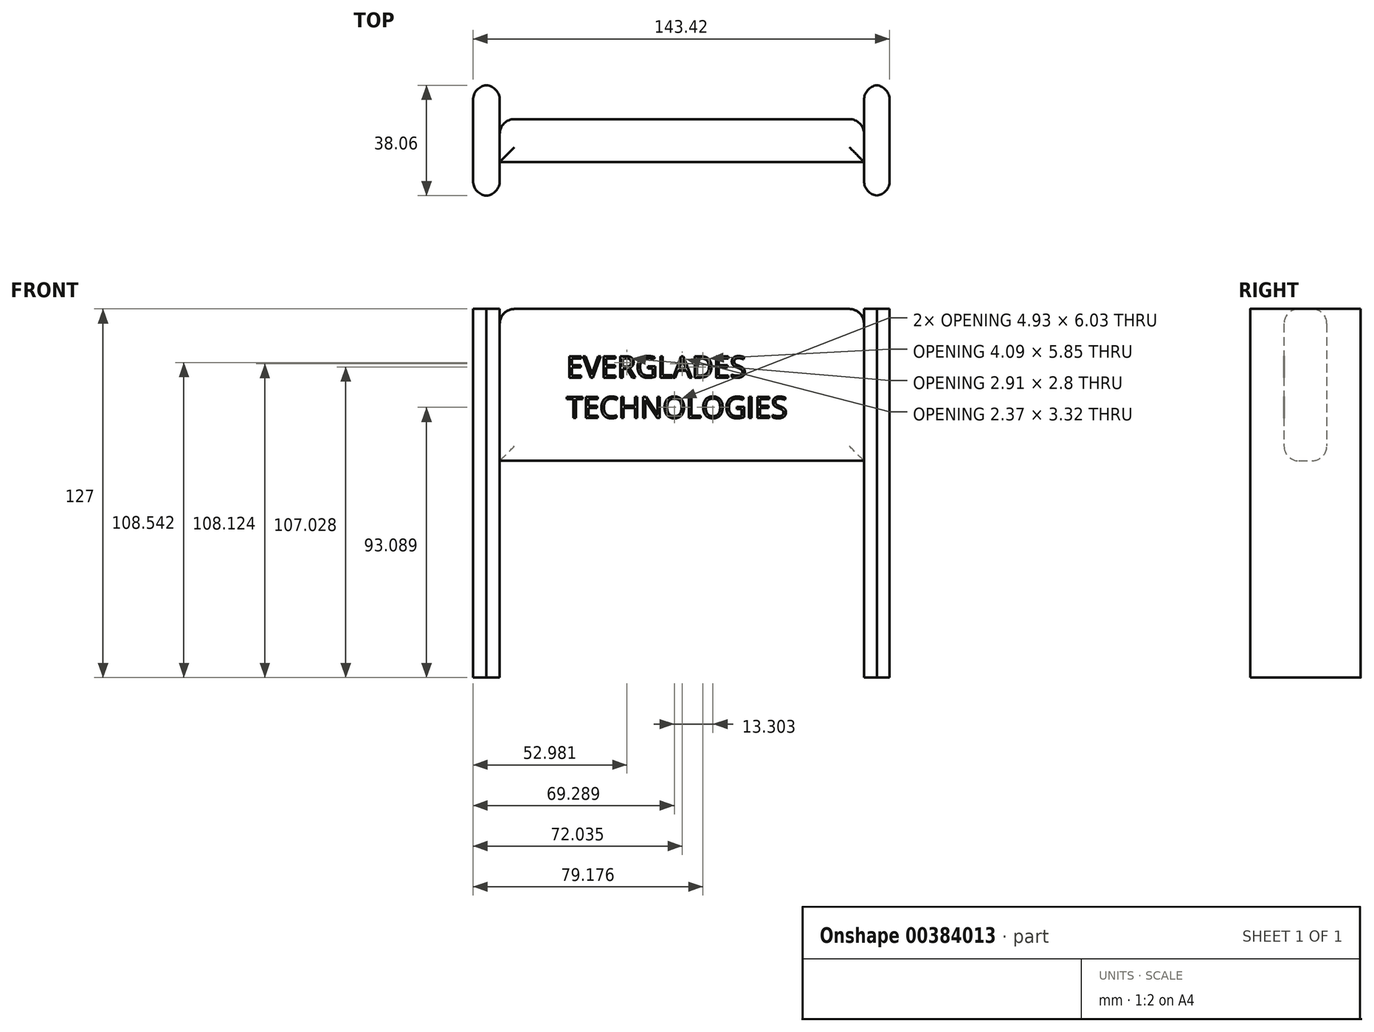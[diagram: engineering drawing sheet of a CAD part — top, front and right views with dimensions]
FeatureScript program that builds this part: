
annotation { "Feature Type Name" : "Feature", "Feature Type Description" : "" }
export const myFeature = defineFeature(function(context is Context, id is Id, definition is map)
    precondition{}
    {
        {
            var Q0;
            Q0=qCreatedBy(makeId("Front.planeOp"),FACE);
            var sketch = newSketch(context, id + "F0", { "sketchPlane" : qUnion([Q0])});
            skLineSegment(sketch, "E0.bottom", {"start": v(-58.02, 63.98) * mm, "end": v(67.38, 63.98) * mm});
            skLineSegment(sketch, "E0.top", {"start": v(-58.02, 11.67) * mm, "end": v(67.38, 11.67) * mm});
            skLineSegment(sketch, "E0.left", {"start": v(-58.02, 63.98) * mm, "end": v(-58.02, 11.67) * mm});
            skLineSegment(sketch, "E0.right", {"start": v(67.38, 63.98) * mm, "end": v(67.38, 11.67) * mm});
            skLineSegment(sketch, "E1", {"start": v(-58.02, 11.67) * mm, "end": v(-58.02, -63.02) * mm});
            skLineSegment(sketch, "E2", {"start": v(-67.23, 63.98) * mm, "end": v(-67.23, -63.02) * mm});
            skLineSegment(sketch, "E3", {"start": v(67.38, 11.67) * mm, "end": v(67.38, -63.02) * mm});
            skLineSegment(sketch, "E4", {"start": v(76.2, 63.98) * mm, "end": v(76.2, -63.02) * mm});
            skLineSegment(sketch, "E5", {"start": v(-67.23, 63.98) * mm, "end": v(-58.02, 63.98) * mm});
            skLineSegment(sketch, "E6", {"start": v(67.38, 63.98) * mm, "end": v(76.2, 63.98) * mm});
            skLineSegment(sketch, "E7", {"start": v(67.38, -63.02) * mm, "end": v(76.2, -63.02) * mm});
            skLineSegment(sketch, "E8", {"start": v(-67.23, -63.02) * mm, "end": v(-58.02, -63.02) * mm});
            skSolve(sketch);
        }
        {
            var Q0;
            Q0=makeQuery(id+"F0.imprint","IMPRINT",FACE,{"disambiguationData":[TD([[makeQuery(id+"F0.imprint","IMPRINT",EDGE,{"derivedFrom":sQuery(id+"F0.wireOp",EDGE,"E0.left")}),-1.0]])]});
            var Q1;
            Q1=makeQuery(id+"F0.imprint","IMPRINT",FACE,{"disambiguationData":[TD([[makeQuery(id+"F0.imprint","IMPRINT",EDGE,{"derivedFrom":sQuery(id+"F0.wireOp",EDGE,"E0.right")}),1.0]])]});
            extrude(context, id + "F1", {"entities" : qUnion([Q0, Q1]), "endBound" : BoundingType.SYMMETRIC, "depth" : 38.1 * mm});
        }
        {
            var Q0;
            Q0=makeQuery(id+"F0.imprint","IMPRINT",FACE,{"disambiguationData":[TD([[makeQuery(id+"F0.imprint","IMPRINT",EDGE,{"derivedFrom":sQuery(id+"F0.wireOp",EDGE,"E0.bottom")}),-1.0]])]});
            extrude(context, id + "F2", {"entities" : qUnion([Q0]), "endBound" : BoundingType.SYMMETRIC, "depth" : 14.73 * mm});
        }
        {
            var Q0;
            Q0=makeQuery(id+"F1.opExtrude","CAP_EDGE",EDGE,{"disambiguationData":[OSD([sQuery(id+"F0.wireOp",EDGE,"E2")])],"isStart":false});
            var Q1;
            Q1=makeQuery(id+"F1.opExtrude","CAP_EDGE",EDGE,{"disambiguationData":[OSD([sQuery(id+"F0.wireOp",EDGE,"E0.left"),sQuery(id+"F0.wireOp",EDGE,"E1")])],"isStart":false});
            var Q2;
            Q2=makeQuery(id+"F2.opExtrude","SWEPT_EDGE",EDGE,{"disambiguationData":[OSD([sQuery(id+"F0.wireOp",EDGE,"E0.bottom"),sQuery(id+"F0.wireOp",EDGE,"E0.left"),sQuery(id+"F0.wireOp",EDGE,"E5")])]});
            var Q3;
            Q3=makeQuery(id+"F2.opExtrude","CAP_EDGE",EDGE,{"disambiguationData":[OSD([sQuery(id+"F0.wireOp",EDGE,"E0.bottom")])],"isStart":false});
            var Q4;
            Q4=makeQuery(id+"F2.opExtrude","CAP_EDGE",EDGE,{"disambiguationData":[OSD([sQuery(id+"F0.wireOp",EDGE,"E0.top")])],"isStart":false});
            var Q5;
            Q5=makeQuery(id+"F1.opExtrude","CAP_EDGE",EDGE,{"disambiguationData":[OSD([sQuery(id+"F0.wireOp",EDGE,"E2")])],"isStart":true});
            var Q6;
            Q6=makeQuery(id+"F1.opExtrude","CAP_EDGE",EDGE,{"disambiguationData":[OSD([sQuery(id+"F0.wireOp",EDGE,"E0.left"),sQuery(id+"F0.wireOp",EDGE,"E1")])],"isStart":true});
            var Q7;
            Q7=makeQuery(id+"F1.opExtrude","CAP_EDGE",EDGE,{"disambiguationData":[OSD([sQuery(id+"F0.wireOp",EDGE,"E4")])],"isStart":false});
            var Q8;
            Q8=makeQuery(id+"F1.opExtrude","CAP_EDGE",EDGE,{"disambiguationData":[OSD([sQuery(id+"F0.wireOp",EDGE,"E0.right"),sQuery(id+"F0.wireOp",EDGE,"E3")])],"isStart":false});
            var Q9;
            Q9=makeQuery(id+"F1.opExtrude","CAP_EDGE",EDGE,{"disambiguationData":[OSD([sQuery(id+"F0.wireOp",EDGE,"E4")])],"isStart":true});
            var Q10;
            Q10=makeQuery(id+"F1.opExtrude","CAP_EDGE",EDGE,{"disambiguationData":[OSD([sQuery(id+"F0.wireOp",EDGE,"E0.right"),sQuery(id+"F0.wireOp",EDGE,"E3")])],"isStart":true});
            var Q11;
            Q11=makeQuery(id+"F2.opExtrude","CAP_EDGE",EDGE,{"disambiguationData":[OSD([sQuery(id+"F0.wireOp",EDGE,"E0.bottom")])],"isStart":true});
            var Q12;
            Q12=makeQuery(id+"F2.opExtrude","CAP_EDGE",EDGE,{"disambiguationData":[OSD([sQuery(id+"F0.wireOp",EDGE,"E0.top")])],"isStart":true});
            var Q13;
            Q13=makeQuery(id+"F2.opExtrude","CAP_EDGE",EDGE,{"disambiguationData":[OSD([sQuery(id+"F0.wireOp",EDGE,"E0.left")])],"isStart":true});
            var Q14;
            Q14=makeQuery(id+"F2.opExtrude","CAP_EDGE",EDGE,{"disambiguationData":[OSD([sQuery(id+"F0.wireOp",EDGE,"E0.right")])],"isStart":true});
            var Q15;
            Q15=makeQuery(id+"F2.opExtrude","SWEPT_EDGE",EDGE,{"disambiguationData":[OSD([sQuery(id+"F0.wireOp",EDGE,"E0.bottom"),sQuery(id+"F0.wireOp",EDGE,"E0.right"),sQuery(id+"F0.wireOp",EDGE,"E6")])]});
            fillet(context, id + "F3", {"entities" : qUnion([Q0, Q1, Q2, Q3, Q4, Q5, Q6, Q7, Q8, Q9, Q10, Q11, Q12, Q13, Q14, Q15]), "radius" : 5.08 * mm, "tangentPropagation" : true, "allowEdgeOverflow" : false});
        }
        {
            var Q0;
            Q0=makeQuery(id+"F2.opExtrude","CAP_FACE",FACE,{"disambiguationData":[OSD([sQuery(id+"F0.wireOp",EDGE,"E0.bottom"),sQuery(id+"F0.wireOp",EDGE,"E0.top"),sQuery(id+"F0.wireOp",EDGE,"E0.left"),sQuery(id+"F0.wireOp",EDGE,"E0.right")])],"isStart":false});
            var sketch = newSketch(context, id + "F4", { "sketchPlane" : qUnion([Q0])});
            skText(sketch, "E9", { "text": "EVERGLADES\nTECHNOLOGIES", "fontName": "OpenSans-Regular.ttf"});
            const initialGuessF4  = {"E9": [-0.03506, 0.04035, 1, 0, 0.00738]};
            skSetInitialGuess(sketch, initialGuessF4);
            skSolve(sketch);
        }
        {
            var Q0;
            Q0 = qSketchRegion(id + "F4", true);
            extrude(context, id + "F5", {"entities" : qUnion([Q0]), "oppositeDirection" : true, "depth" : 0.03 * mm});
        }
    });
